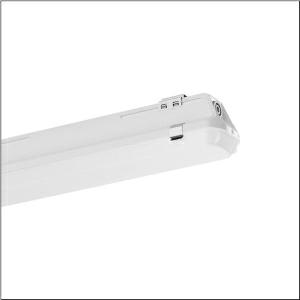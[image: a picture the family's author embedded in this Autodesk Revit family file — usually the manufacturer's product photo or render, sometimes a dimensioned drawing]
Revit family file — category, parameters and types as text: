
# Revit family: monsun_r__21_51fb107p460b_c23d
name_source: partatom
category: Lighting Fixtures
units: mm (PartAtom-declared; Revit-internal decimal feet)

## family parameters
Cut with Voids When Loaded = No
Host = Face
Light Source = No
Part Type = Normal
Room Calculation Point = No
Round Connector Dimension = Use Diameter
Shared = No

## types (1)
- Monsun® 21 (1 x LED, 6000 lm, 38 W, 4000K)
    Apparent Load = 38 VA
    CIE Flux Codes = 47 77 93 94 100
    Color Rendering = 80
    Color Temperature = 4000K
    Default Elevation = 1800 mm
    Description = Monsun® 21, damp-proof luminaire, chain hanger, primary optical cover: enclosure, of PMMA, light emission: direct distribution, primary light characteristic: symmetric, installation type: suspended mounting, surface-mounted, horizontal mounting, vertical mounting, LED, rated luminous flux: 6.000lm, luminous efficacy: 158lm/W, light colour: 840, colour temperature: 4000K, control gear: ECG, with terminal, 3-pole, max. 2.5mm², mains connection: 220..240V, AC, 50/60Hz, rated input power: 38W, housing, of glass-fibre reinforced polyester, uncoated, bright grey, incl. chain hanger, length: 1.590mm, width: 90mm, height: 88mm, clip for enclosure, of stainless steel (V2A), ceiling mounting element, of stainless steel (V2A), chain hanger, of stainless steel (V2A), protection rating (complete): IP66, insulation class (complete): insulation class I (protective earthing), certification: CE, ENEC, VDE, UKCA, protection symbol: D, impact resistance: IK04, permissible operating ambient temperature: -25..+35°C, standard: EN 50419, EN 60598-2-1, corresponds to IFS (International Featured Standards) requirements for safety and quality in the food industry, for indoor or canopied outdoor use, no direct snow, no direct sun, no direct rain, contact your sales advisor before using the luminaires in applications with unclear chemical exposure, large temperature fluctuations or condensation-forming humidity, LABS conformity tested according to VDMA 24364:2018-05, packaging unit: 1 piece
    Height = 89 mm
    Lamp = 1 x LED
    Lamp Light Flux = 6000 lm
    Lamp Power = 38 W
    Lamp count = 1
    Length = 1590 mm
    Luminous efficacy = 158 lm/W
    Manufacturer = Siteco
    ModVariant = No
    Model = 51FB107P460B
    Mounting Place = Ceiling
    Mounting Type = Surface mounted
    Number of Poles = 1
    OnlyDefault = Yes
    Power Factor = 1
    Product Name = Monsun® 21
    Product group = damp-proof luminaire
    ProductGroupID = 300
    Protection Class = Protection class I
    Protection Degree = IP 66
    RLX_Detail_Level = 1
    RLX_Emergency_Light_Flux = 0 lm
    RLX_Emergency_Type = 0
    RLX_Emergency_Type_DB = No
    RlxData = <blob elided: 88561 chars, md5=ebf5dd96>
    Socket = socket
    Standby Power = 0 W
    System Light Flux = 6000 lm
    System Power = 38 W
    Type Comments = Product without accessories
    Type Image = l_1319656.jpg
    URL = http://relux.com
    VarID = ---
    Voltage = 0 V
    Weight = 0.00 kg
    Width = 90 mm

## geometry (parser evidence)
native form markers: Blend x4, Sweep x11
no freeform markers — native parametric forms only
